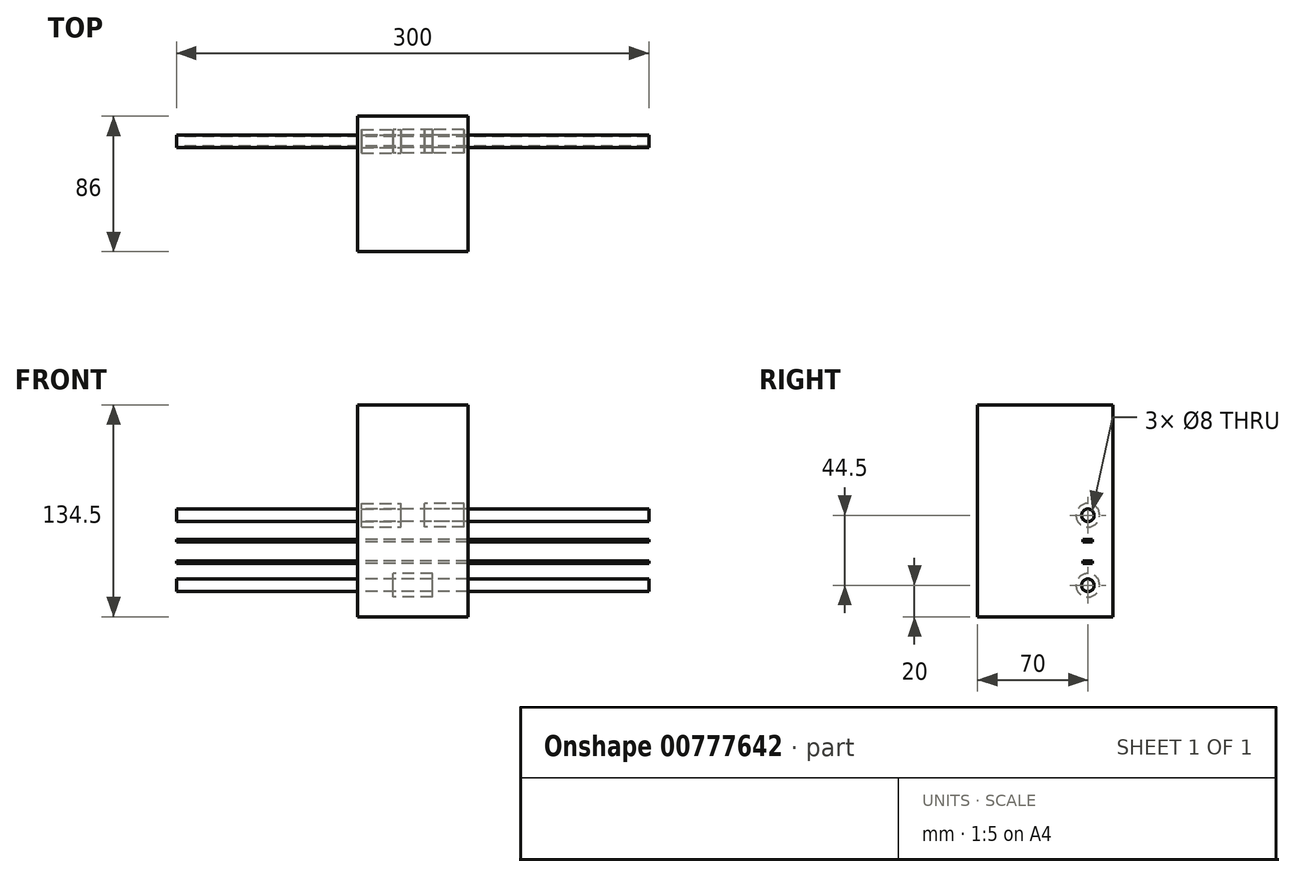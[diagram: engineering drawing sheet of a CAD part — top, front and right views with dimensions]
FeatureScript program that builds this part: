
annotation { "Feature Type Name" : "Feature", "Feature Type Description" : "" }
export const myFeature = defineFeature(function(context is Context, id is Id, definition is map)
    precondition{}
    {
        {
            var Q0;
            Q0=qCreatedBy(makeId("Right.planeOp"),FACE);
            var sketch = newSketch(context, id + "F0", { "sketchPlane" : qUnion([Q0])});
            skCircle(sketch, "E0", {"center": v(0, 0) * mm, "radius": 4 * mm});
            skCircle(sketch, "E1", {"center": v(0, 44.5) * mm, "radius": 4 * mm});
            skLineSegment(sketch, "E2.bottom", {"start": v(-3, 15.5) * mm, "end": v(3, 15.5) * mm});
            skLineSegment(sketch, "E2.top", {"start": v(-3, 14) * mm, "end": v(3, 14) * mm});
            skLineSegment(sketch, "E2.left", {"start": v(-3, 15.5) * mm, "end": v(-3, 14) * mm});
            skLineSegment(sketch, "E2.right", {"start": v(3, 15.5) * mm, "end": v(3, 14) * mm});
            skLineSegment(sketch, "E3.bottom", {"start": v(-3, 29) * mm, "end": v(3, 29) * mm});
            skLineSegment(sketch, "E3.top", {"start": v(-3, 27.5) * mm, "end": v(3, 27.5) * mm});
            skLineSegment(sketch, "E3.left", {"start": v(-3, 29) * mm, "end": v(-3, 27.5) * mm});
            skLineSegment(sketch, "E3.right", {"start": v(3, 29) * mm, "end": v(3, 27.5) * mm});
            skSolve(sketch);
        }
        {
            var Q0;
            Q0 = qSketchRegion(id + "F0", true);
            extrude(context, id + "F1", {"entities" : qUnion([Q0]), "depth" : 300 * mm, "offsetDistance" : 25 * mm, "symmetric" : true});
        }
        {
            var Q0;
            Q0=qCreatedBy(makeId("Right.planeOp"),FACE);
            var sketch = newSketch(context, id + "F2", { "sketchPlane" : qUnion([Q0])});
            skLineSegment(sketch, "E4.bottom", {"start": v(-70, 114.5) * mm, "end": v(16, 114.5) * mm});
            skLineSegment(sketch, "E4.top", {"start": v(-70, -20) * mm, "end": v(16, -20) * mm});
            skLineSegment(sketch, "E4.left", {"start": v(-70, 114.5) * mm, "end": v(-70, -20) * mm});
            skLineSegment(sketch, "E4.right", {"start": v(16, 114.5) * mm, "end": v(16, -20) * mm});
            skSolve(sketch);
        }
        {
            var Q0;
            Q0 = qSketchRegion(id + "F2", true);
            extrude(context, id + "F3", {"entities" : qUnion([Q0]), "depth" : 70 * mm, "offsetDistance" : 25 * mm, "symmetric" : true});
        }
        {
            var Q0;
            Q0=qCreatedBy(makeId("Right.planeOp"),FACE);
            var sketch = newSketch(context, id + "F4", { "sketchPlane" : qUnion([Q0])});
            skCircle(sketch, "E5", {"center": v(0, 0) * mm, "radius": 4 * mm});
            skCircle(sketch, "E6", {"center": v(0, 0) * mm, "radius": 7.5 * mm});
            skSolve(sketch);
        }
        {
            var Q0;
            Q0 = qSketchRegion(id + "F4", true);
            extrude(context, id + "F5", {"entities" : qUnion([Q0]), "depth" : 25 * mm, "offsetDistance" : 25 * mm, "symmetric" : true});
        }
        {
            var Q0;
            Q0=makeQuery(id+"F5.opExtrude","SWEPT_BODY",BODY,{"disambiguationData":[OSD([sQuery(id+"F4.wireOp",EDGE,"E5"),sQuery(id+"F4.wireOp",EDGE,"E6")])]});
            transform(context, id + "F6", {"entities" : qUnion([Q0]), "transformType" : TransformType.TRANSLATION_3D, "dx" : 20 * mm, "dy" : 0 * mm, "dz" : 44.5 * mm, "makeCopy" : true});
        }
        {
            var Q0;
            Q0=makeQuery(id+"F6.opPattern","COPY",BODY,{"derivedFrom":makeQuery(id+"F5.opExtrude","SWEPT_BODY",BODY,{"disambiguationData":[OSD([sQuery(id+"F4.wireOp",EDGE,"E5"),sQuery(id+"F4.wireOp",EDGE,"E6")])]}),"instanceName":"1"});
            var Q1;
            Q1=qCreatedBy(makeId("Right.planeOp"),FACE);
            mirror(context, id + "F7", {"entities" : qUnion([Q0]), "mirrorPlane" : qUnion([Q1])});
        }
    });
